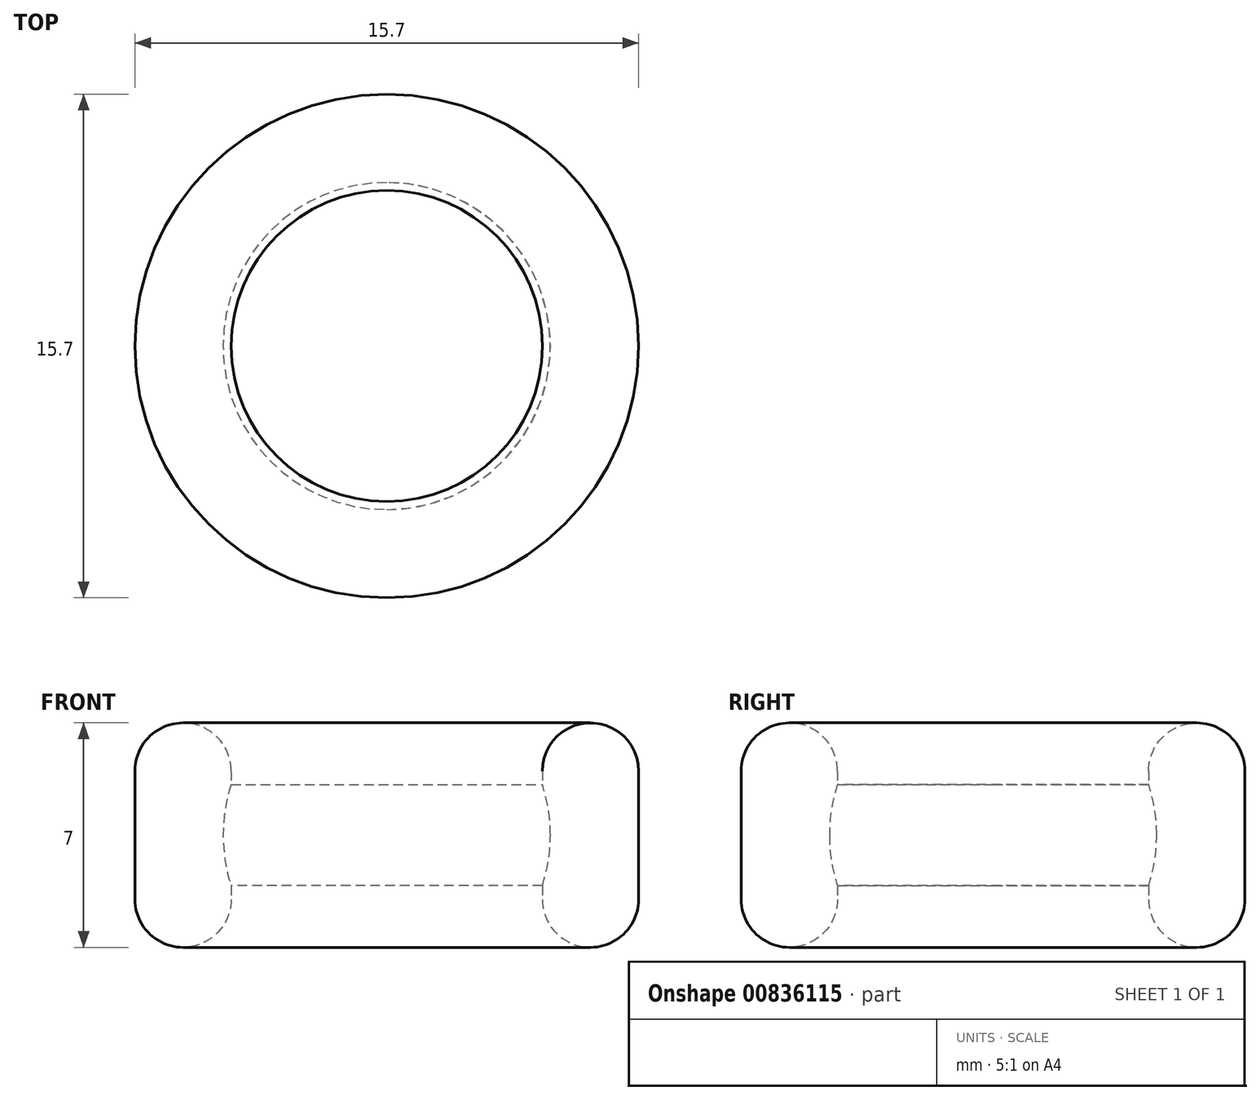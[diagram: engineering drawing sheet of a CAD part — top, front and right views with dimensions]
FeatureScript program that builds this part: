
annotation { "Feature Type Name" : "Feature", "Feature Type Description" : "" }
export const myFeature = defineFeature(function(context is Context, id is Id, definition is map)
    precondition{}
    {
        {
            var Q0;
            Q0=qCreatedBy(makeId("Top.planeOp"),FACE);
            var sketch = newSketch(context, id + "F0", { "sketchPlane" : qUnion([Q0])});
            skCircle(sketch, "E0", {"center": v(0, 0) * mm, "radius": 4.85 * mm});
            skArc(sketch, "E1", {"start": v(0, -5.1) * mm, "mid": v(5.1, 0) * mm, "end": v(0, 5.1) * mm});
            skCircle(sketch, "E2", {"center": v(0, 0) * mm, "radius": 7.85 * mm});
            skLineSegment(sketch, "E3", {"start": v(0, 11.04) * mm, "end": v(0, -8.95) * mm, "construction": true});
            skLineSegment(sketch, "E4", {"start": v(0, 5.1) * mm, "end": v(0, -5.1) * mm});
            skSolve(sketch);
        }
        {
            var Q0;
            Q0=makeQuery(id+"F0.imprint","IMPRINT",FACE,{"disambiguationData":[TD([[makeQuery(id+"F0.imprint","IMPRINT",EDGE,{"derivedFrom":sQuery(id+"F0.wireOp",EDGE,"E0")}),-1.0]])]});
            var Q1;
            Q1=makeQuery(id+"F0.imprint","IMPRINT",FACE,{"disambiguationData":[TD([[makeQuery(id+"F0.imprint","IMPRINT",EDGE,{"derivedFrom":sQuery(id+"F0.wireOp",EDGE,"E1")}),-1.0]])]});
            extrude(context, id + "F1", {"entities" : qUnion([Q0, Q1]), "endBound" : BoundingType.SYMMETRIC, "depth" : 7 * mm, "offsetDistance" : 25 * mm});
        }
        {
            var Q0;
            {var subQ0=sQuery(id+"F0.wireOp",EDGE,"E4");var subQ1=sQuery(id+"F0.wireOp",EDGE,"E0");var subQ2=makeQuery(id+"F0.imprint","INTERSECT",VERTEX,{"disambiguationData":[OD(0.0)],"derivedFrom":[subQ1,subQ0]});Q0=makeQuery(id+"F0.imprint","IMPRINT",FACE,{"disambiguationData":[TD([[makeQuery(id+"F0.imprint","IMPRINT",EDGE,{"disambiguationData":[TD([[subQ2,1.0]])],"derivedFrom":subQ1}),1.0]])]});}
            var Q1;
            {var subQ4=sQuery(id+"F0.wireOp",EDGE,"E1");Q1=makeQuery(id+"F0.imprint","IMPRINT",FACE,{"disambiguationData":[TD([[makeQuery(id+"F0.imprint","IMPRINT",EDGE,{"derivedFrom":subQ4}),1.0]])]});}
            var Q2;
            Q2=sQuery(id+"F0.wireOp",EDGE,"E4");
            revolve(context, id + "F2", {"operationType" : NewBodyOperationType.REMOVE, "surfaceOperationType" : NewSurfaceOperationType.NEW, "entities" : qUnion([Q0, Q1]), "axis" : qUnion([Q2]), "revolveType" : RevolveType.FULL});
        }
        {
            var Q0;
            Q0=makeQuery(id+"F1.opExtrude","CAP_EDGE",EDGE,{"disambiguationData":[OSD([sQuery(id+"F0.wireOp",EDGE,"E2")])],"isStart":false});
            var Q1;
            Q1=makeQuery(id+"F1.opExtrude","CAP_EDGE",EDGE,{"disambiguationData":[OSD([sQuery(id+"F0.wireOp",EDGE,"E0")])],"isStart":false});
            var Q2;
            Q2=makeQuery(id+"F1.opExtrude","CAP_EDGE",EDGE,{"disambiguationData":[OSD([sQuery(id+"F0.wireOp",EDGE,"E0")])],"isStart":true});
            var Q3;
            Q3=makeQuery(id+"F1.opExtrude","CAP_EDGE",EDGE,{"disambiguationData":[OSD([sQuery(id+"F0.wireOp",EDGE,"E2")])],"isStart":true});
            fillet(context, id + "F3", {"entities" : qUnion([Q0, Q1, Q2, Q3]), "radius" : 1.5 * mm, "tangentPropagation" : true, "allowEdgeOverflow" : false});
        }
    });
